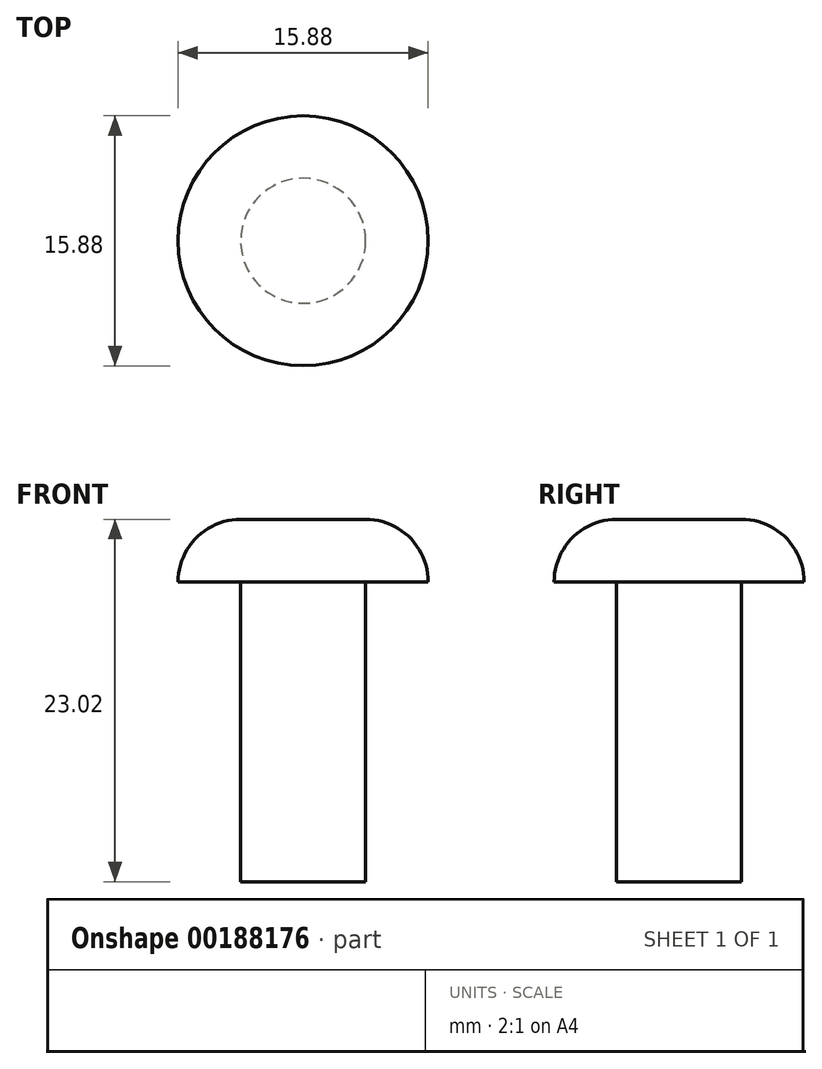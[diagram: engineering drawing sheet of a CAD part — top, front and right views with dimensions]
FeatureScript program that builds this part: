
annotation { "Feature Type Name" : "Feature", "Feature Type Description" : "" }
export const myFeature = defineFeature(function(context is Context, id is Id, definition is map)
    precondition{}
    {
        {
            var Q0;
            Q0=qCreatedBy(makeId("Front.planeOp"),FACE);
            var sketch = newSketch(context, id + "F0", { "sketchPlane" : qUnion([Q0])});
            skLineSegment(sketch, "E0", {"start": v(0, 0) * mm, "end": v(3.97, 0) * mm});
            skLineSegment(sketch, "E1", {"start": v(3.97, 0) * mm, "end": v(3.97, 19.05) * mm});
            skLineSegment(sketch, "E2", {"start": v(3.97, 19.05) * mm, "end": v(7.94, 19.05) * mm});
            skLineSegment(sketch, "E3", {"start": v(0, 0) * mm, "end": v(0, 23.02) * mm});
            skLineSegment(sketch, "E4", {"start": v(0, 23.02) * mm, "end": v(3.97, 23.02) * mm});
            skLineSegment(sketch, "E5", {"start": v(0, 29.75) * mm, "end": v(0, -8.62) * mm, "construction": true});
            skArc(sketch, "E6", {"start": v(7.94, 19.05) * mm, "mid": v(6.78, 21.86) * mm, "end": v(3.97, 23.02) * mm});
            skSolve(sketch);
        }
        {
            var Q0;
            Q0=makeQuery(id+"F0.imprint","IMPRINT",FACE,{"disambiguationData":[TD([[makeQuery(id+"F0.imprint","IMPRINT",EDGE,{"derivedFrom":sQuery(id+"F0.wireOp",EDGE,"E0")}),1.0]])]});
            var Q1;
            Q1=sQuery(id+"F0.wireOp",EDGE,"E5");
            revolve(context, id + "F1", {"entities" : qUnion([Q0]), "axis" : qUnion([Q1]), "revolveType" : RevolveType.FULL});
        }
    });
